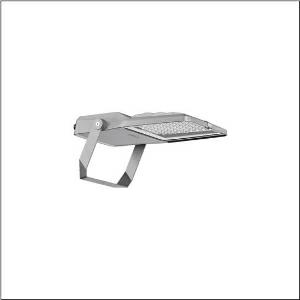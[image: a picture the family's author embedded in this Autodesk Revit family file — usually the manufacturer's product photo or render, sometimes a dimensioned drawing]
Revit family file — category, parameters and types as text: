
# Revit family: floodlight_fl_21_iq_mini___rs12_5xa7771d4b1a_77d6
name_source: partatom
category: Lighting Fixtures
units: mm (PartAtom-declared; Revit-internal decimal feet)

## family parameters
Cut with Voids When Loaded = No
Host = Face
Light Source = No
Part Type = Normal
Room Calculation Point = No
Round Connector Dimension = Use Diameter
Shared = No

## types (1)
- --- (1 x LED, 18810 lm, 143 W, 4000K)
    Apparent Load = 143 VA
    CIE Flux Codes = 79 92 99 100 100
    Color Rendering = 70
    Color Temperature = 4000K
    Default Elevation = 1800 mm
    Description = Floodlight FL 21 iQ mini, floodlight, primary light control with lens, of PMMA, primary optical cover: protective disc, of toughened safety glass, transparent, light distribution: RS12, light emission: direct distribution, installation type: surface-mounted, lamps: LED, High Power LED, rated values: 18.810lm | 143W | 131,5lm/W (begin service life); end service life: 18.810lm | 151,6W; at 50% lumin. flux: 9.405lm | 60,8W | 154,7lm/W, colour temperature: 4000K, colour rendering: CRI > 70, light colour: 740, light setting 1 begin service life: 100% | 18.810lm | 143W | 131,5lm/W | 4.000K, light setting 1 end service life: 151,6W, further light settings possible, control: Auto-Match, Temp-Guard, Lumen-Switch, Night-Set, Smart-Wire, Light-Fading, Desk-Remote (wireless, voltage-free reading and setting of iQ features in the workshop via application-optimized NFC function/RFID function), optimised constant luminous flux control (CLO 2.0), pre-setting: linear dimming characteristic, with terminal, 6-pole, mains connection: 220..240V, AC, 50/60Hz, luminaire housing, of diecast aluminium, powder-coated, SITECO metallic grey (DB 702S), corrosivity category C5 mid according to DIN EN ISO 12944suitable for swimming poolschlorine-resistant, sealing non-destructively replaceable, mounting bracket, of steel, galvanised, powder-coated, SITECO metallic grey (DB 702S), protection rating (complete): IP66, insulation class (complete): insulation class II (safety insulation), certification: CE, ENEC, VDE, protection symbol: D, impact resistance: IK08, permissible operating ambient temperature: -40..+40°C, permissible operating ambient temperature for outdoor applications: -40..+50°C, standard: DIN EN 12944, LABS conformity tested according to VDMA 24364:2018-05, packaging unit: 1 piece

Light Distribution: RS12
    Height = 70 mm
    Lamp = 1 x LED
    Lamp Light Flux = 18810 lm
    Lamp Power = 143 W
    Lamp count = 1
    Length = 485 mm
    Luminous efficacy = 132 lm/W
    Manufacturer = Siteco
    ModVariant = No
    Model = 5XA7771D4B1A
    Number of Poles = 1
    OnlyDefault = Yes
    Power Factor = 1
    Product Name = Floodlight FL 21 iQ mini | RS12
    Product group = floodlight | pylon annexe
    ProductGroupID = 6201
    Protection Class = Protection class II
    Protection Degree = IP 66
    RLX_Detail_Level = 1
    RLX_Emergency_Light_Flux = 0 lm
    RLX_Emergency_Type = 0
    RLX_Emergency_Type_DB = No
    RlxData = <blob elided: 91581 chars, md5=09e0dd0a>
    Socket = socket
    Standby Power = 0 W
    System Light Flux = 18810 lm
    System Power = 143 W
    Type Comments = factory setting: luminous flux: 100 % | dim-lin: 254 | 730 mA
    Type Image = l_1006845.jpg
    URL = http://relux.com
    VarID = @adj_166929
    Voltage = 0 V
    Weight = 0.00 kg
    Width = 337 mm

## geometry (parser evidence)
native form markers: Blend x4, Sweep x12
no freeform markers — native parametric forms only
